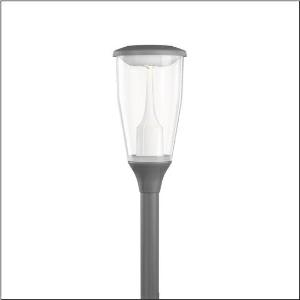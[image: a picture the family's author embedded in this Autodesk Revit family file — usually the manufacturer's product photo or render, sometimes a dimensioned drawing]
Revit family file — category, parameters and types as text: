
# Revit family: dl_11_iq___st1_2a_5xa5575mf14h000022_93a8
name_source: partatom
category: Lighting Fixtures
units: mm (PartAtom-declared; Revit-internal decimal feet)

## family parameters
Cut with Voids When Loaded = No
Host = Face
Light Source = No
Part Type = Normal
Room Calculation Point = No
Round Connector Dimension = Use Diameter
Shared = No

## types (1)
- --- (1 x LED, 1560 lm, 11.8 W, 2700K)
    Apparent Load = 12 VA
    CIE Flux Codes = 24 63 94 96 100
    Color Rendering = 70
    Color Temperature = 2700K
    Default Elevation = 1800 mm
    Description = DL 11 iQ, mast luminaire, Module 540 iQ-SR, primary light control with 3 zone facetted reflector, of plastic, silver coated, highly specular, structured, primary optical cover: cover, of PMMA, transparent, light distribution: ST1.2a, light emission: direct distribution, primary light characteristic: asymmetric, installation type: post-top, LED, High Power LED, rated luminous flux: 1.560lm, luminous efficacy: 149lm/W, light colour: 727, colour temperature: 2700K, control: Street-Remote, Auto-Match, Temp-Guard, Lumen-Switch, Night-Set, Smart-Wire, Light-Fading, Desk-Remote (wireless, voltage-free reading and setting of iQ features in the workshop via application-optimized NFC function/RFID function), optimised constant luminous flux control (CLO 2.0), mains connection: 220..240V, AC, 50/60Hz, connection cable pre-assembled, cable length: 5,5m, wiring characteristics: H07RN-F, 5-core, 1.5mm², start of lifetime: 12W, end of service life: 12W, reduction: 5W, luminaire housing, upper part, of diecast aluminium, coated, Siteco® metallic grey (DB 702S), spigot size: 76mm (post-top), post-top mast mounting element, of diecast aluminium, coated, Siteco® metallic grey (DB 702S), Module 540 iQ-SR, traffic white (RAL 9016), equipment: standard, protection rating (complete): IP66, insulation class (complete): insulation class II (safety insulation), certification: CE, ENEC, ENEC+, VDE, packaging unit: 1 piece

Light Distribution: ST1.2a
    Height = 665 mm
    Lamp = 1 x LED
    Lamp Light Flux = 1560 lm
    Lamp Power = 11.8 W
    Lamp count = 1
    Length = 334 mm
    Luminous efficacy = 132 lm/W
    Manufacturer = Siteco
    ModVariant = No
    Model = 5XA5575MF14H000022
    Number of Poles = 1
    OnlyDefault = Yes
    Power Factor = 1
    Product Name = DL 11 iQ | ST1.2a
    Product group = mast luminaire | pylon top
    ProductGroupID = 6100
    Protection Class = Protection class II
    Protection Degree = IP 66
    RLX_Detail_Level = 1
    RLX_Emergency_Light_Flux = 0 lm
    RLX_Emergency_Type = 0
    RLX_Emergency_Type_DB = No
    RlxData = <blob elided: 153429 chars, md5=e51e2f9d>
    Socket = socket
    Standby Power = 0 W
    System Light Flux = 1560 lm
    System Power = 12 W
    Type Comments = factory setting: luminous flux: 100 % | dim-lin: 254 | 472 mA
    Type Image = l_1258354.jpg
    URL = http://relux.com
    VarID = @adj_025709
    Voltage = 0 V
    Weight = 0.00 kg
    Width = 0 mm  [stored 0 ft]

note: [stored X ft] marks values corroborated as IEEE doubles in the binary element streams (Revit-internal decimal feet)

## geometry (parser evidence)
native form markers: Blend x4, Sweep x9
no freeform markers — native parametric forms only
